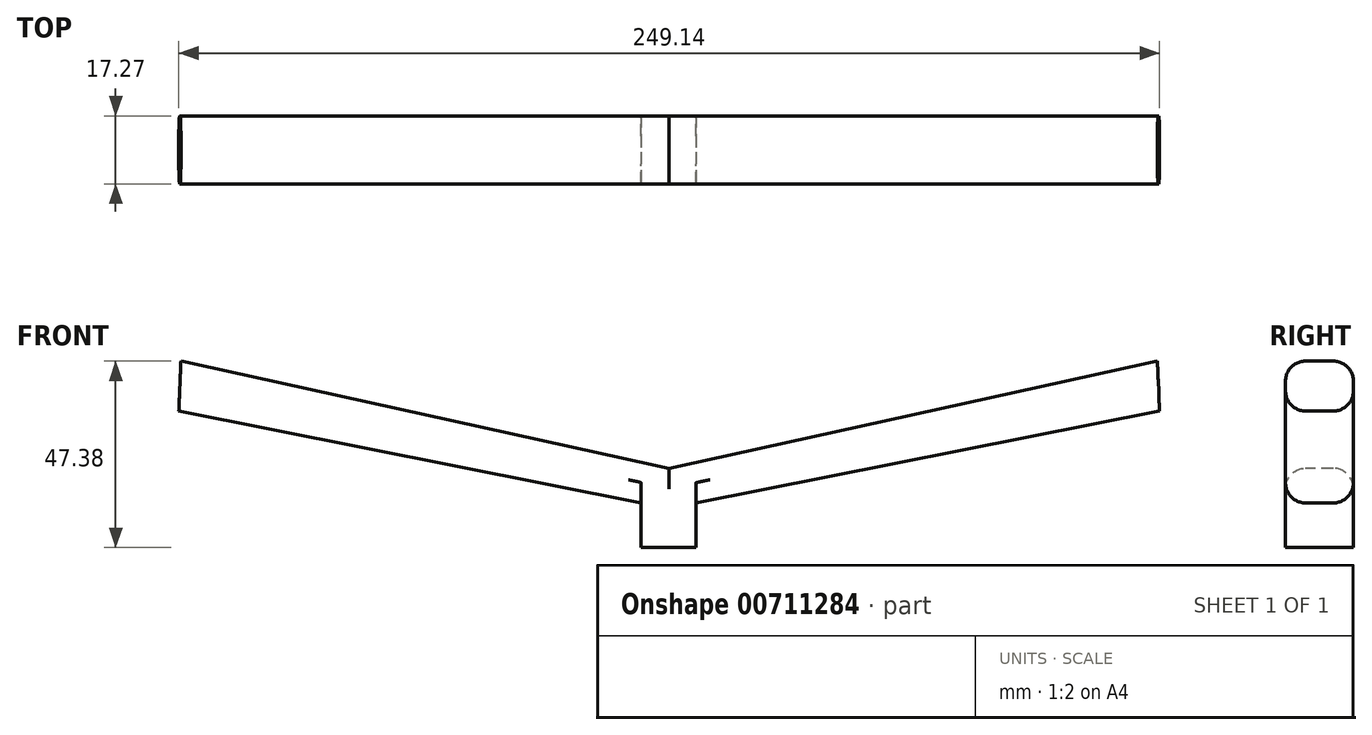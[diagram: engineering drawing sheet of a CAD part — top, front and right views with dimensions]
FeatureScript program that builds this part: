
annotation { "Feature Type Name" : "Feature", "Feature Type Description" : "" }
export const myFeature = defineFeature(function(context is Context, id is Id, definition is map)
    precondition{}
    {
        {
            var Q0;
            Q0=qCreatedBy(makeId("Front.planeOp"),FACE);
            var sketch = newSketch(context, id + "F0", { "sketchPlane" : qUnion([Q0])});
            skLineSegment(sketch, "E0", {"start": v(-182.2, 87.58) * mm, "end": v(-58.16, 60.34) * mm});
            skLineSegment(sketch, "E1", {"start": v(-58.16, 60.34) * mm, "end": v(65.89, 87.58) * mm});
            skLineSegment(sketch, "E2", {"start": v(65.89, 87.58) * mm, "end": v(66.41, 74.9) * mm});
            skLineSegment(sketch, "E3", {"start": v(66.41, 74.9) * mm, "end": v(-58.16, 50.18) * mm});
            skLineSegment(sketch, "E4", {"start": v(-58.16, 50.18) * mm, "end": v(-182.73, 74.9) * mm});
            skLineSegment(sketch, "E5", {"start": v(-182.73, 74.9) * mm, "end": v(-182.2, 87.58) * mm});
            skLineSegment(sketch, "E6.bottom", {"start": v(-65.25, 40.2) * mm, "end": v(-51.34, 40.2) * mm});
            skLineSegment(sketch, "E6.top", {"start": v(-65.25, 57.42) * mm, "end": v(-51.34, 57.42) * mm});
            skLineSegment(sketch, "E6.left", {"start": v(-65.25, 40.2) * mm, "end": v(-65.25, 57.42) * mm});
            skLineSegment(sketch, "E6.right", {"start": v(-51.34, 40.2) * mm, "end": v(-51.34, 57.42) * mm});
            skSolve(sketch);
        }
        {
            var Q0;
            Q0 = qSketchRegion(id + "F0", true);
            var Q1;
            Q1=makeQuery(id+"F0.imprint","IMPRINT",FACE,{"disambiguationData":[TD([[makeQuery(id+"F0.imprint","IMPRINT",EDGE,{"derivedFrom":sQuery(id+"F0.wireOp",EDGE,"E0")}),-1.0]])]});
            extrude(context, id + "F1", {"entities" : qUnion([Q0, Q1]), "oppositeDirection" : true, "depth" : 17.27 * mm, "offsetDistance" : 25.4 * mm});
        }
        {
            var Q0;
            Q0=makeQuery(id+"F1.opExtrude","CAP_EDGE",EDGE,{"disambiguationData":[OSD([sQuery(id+"F0.wireOp",EDGE,"E4")])],"isStart":false});
            var Q1;
            Q1=makeQuery(id+"F1.opExtrude","CAP_EDGE",EDGE,{"disambiguationData":[OSD([sQuery(id+"F0.wireOp",EDGE,"E4")])],"isStart":true});
            var Q2;
            Q2=makeQuery(id+"F1.opExtrude","CAP_EDGE",EDGE,{"disambiguationData":[OSD([sQuery(id+"F0.wireOp",EDGE,"E3")])],"isStart":false});
            var Q3;
            Q3=makeQuery(id+"F1.opExtrude","CAP_EDGE",EDGE,{"disambiguationData":[OSD([sQuery(id+"F0.wireOp",EDGE,"E3")])],"isStart":true});
            var Q4;
            Q4=makeQuery(id+"F1.opExtrude","CAP_EDGE",EDGE,{"disambiguationData":[OSD([sQuery(id+"F0.wireOp",EDGE,"E0")])],"isStart":false});
            var Q5;
            Q5=makeQuery(id+"F1.opExtrude","CAP_EDGE",EDGE,{"disambiguationData":[OSD([sQuery(id+"F0.wireOp",EDGE,"E0")])],"isStart":true});
            var Q6;
            Q6=makeQuery(id+"F1.opExtrude","CAP_EDGE",EDGE,{"disambiguationData":[OSD([sQuery(id+"F0.wireOp",EDGE,"E1")])],"isStart":true});
            var Q7;
            Q7=makeQuery(id+"F1.opExtrude","CAP_EDGE",EDGE,{"disambiguationData":[OSD([sQuery(id+"F0.wireOp",EDGE,"E1")])],"isStart":false});
            fillet(context, id + "F2", {"entities" : qUnion([Q0, Q1, Q2, Q3, Q4, Q5, Q6, Q7]), "radius" : 5.08 * mm, "tangentPropagation" : true, "allowEdgeOverflow" : false});
        }
    });
